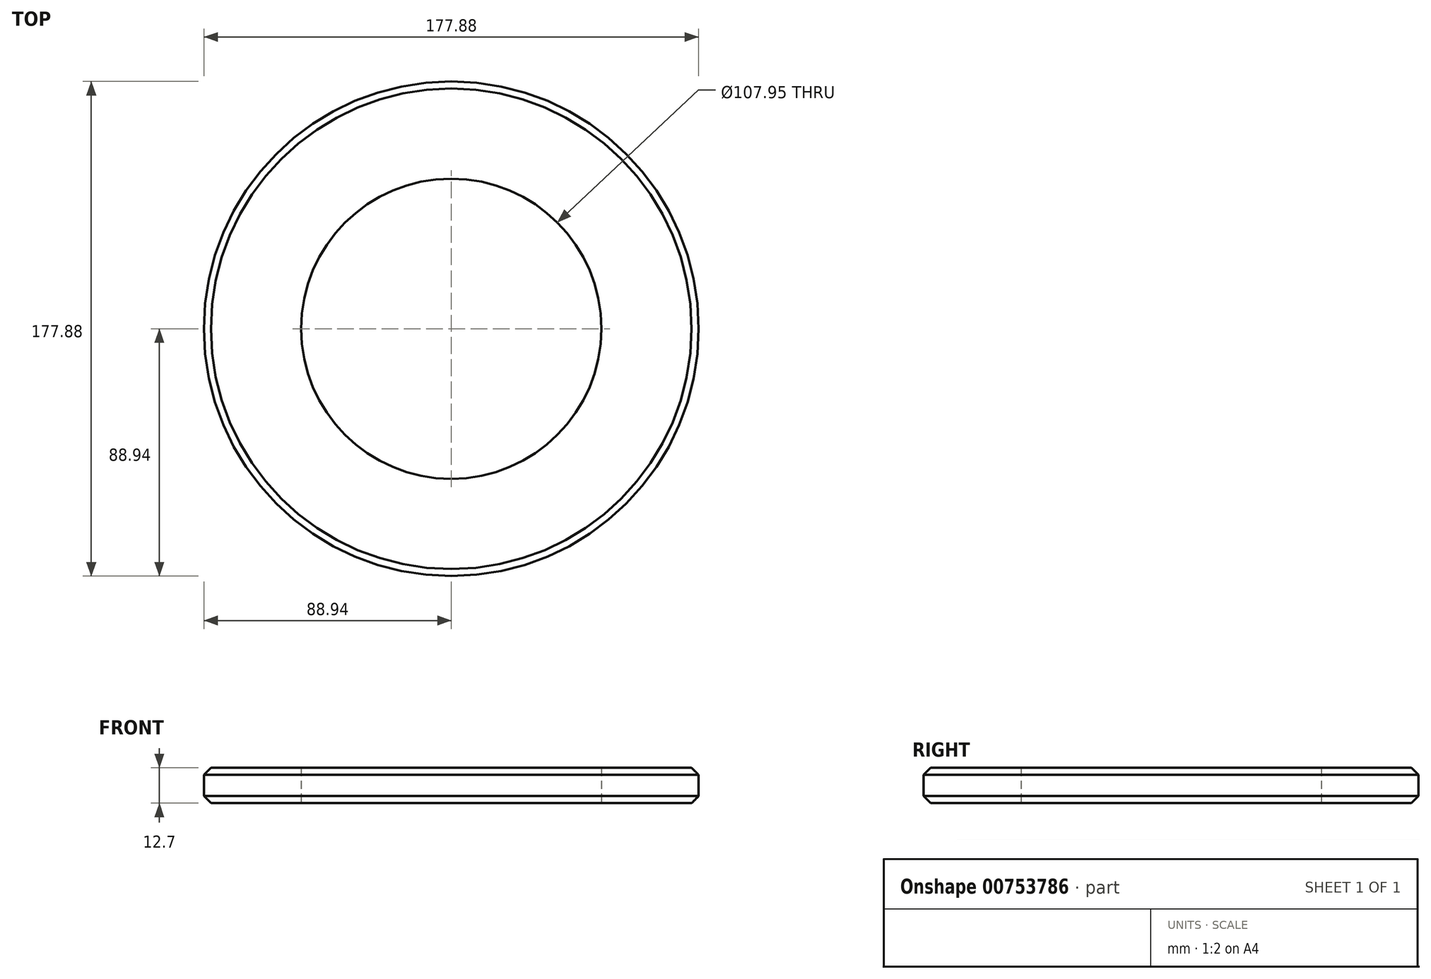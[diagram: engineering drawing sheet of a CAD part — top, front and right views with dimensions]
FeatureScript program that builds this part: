
annotation { "Feature Type Name" : "Feature", "Feature Type Description" : "" }
export const myFeature = defineFeature(function(context is Context, id is Id, definition is map)
    precondition{}
    {
        {
            var Q0;
            Q0=qCreatedBy(makeId("Top.planeOp"),FACE);
            var sketch = newSketch(context, id + "F0", { "sketchPlane" : qUnion([Q0])});
            skCircle(sketch, "E0", {"center": v(0, 0) * mm, "radius": 88.94 * mm});
            skSolve(sketch);
        }
        {
            var Q0;
            Q0 = qSketchRegion(id + "F0", true);
            extrude(context, id + "F1", {"entities" : qUnion([Q0]), "depth" : 12.7 * mm, "offsetDistance" : 25.4 * mm});
        }
        {
            var Q0;
            Q0=makeQuery(id+"F1.opExtrude","CAP_EDGE",EDGE,{"disambiguationData":[OSD([sQuery(id+"F0.wireOp",EDGE,"E0")])],"isStart":false});
            chamfer(context, id + "F2", {"entities" : qUnion([Q0]), "width" : 2.54 * mm, "tangentPropagation" : true});
        }
        {
            var Q0;
            Q0=makeQuery(id+"F1.opExtrude","CAP_EDGE",EDGE,{"disambiguationData":[OSD([sQuery(id+"F0.wireOp",EDGE,"E0")])],"isStart":true});
            chamfer(context, id + "F3", {"entities" : qUnion([Q0]), "width" : 2.54 * mm, "tangentPropagation" : true});
        }
        {
            var Q0;
            Q0=qCreatedBy(makeId("Top.planeOp"),FACE);
            var sketch = newSketch(context, id + "F4", { "sketchPlane" : qUnion([Q0])});
            skCircle(sketch, "E1", {"center": v(0, 0) * mm, "radius": 53.98 * mm});
            skSolve(sketch);
        }
        {
            var Q0;
            Q0 = qSketchRegion(id + "F4", true);
            extrude(context, id + "F5", {"entities" : qUnion([Q0]), "operationType" : NewBodyOperationType.REMOVE, "depth" : 50.8 * mm, "offsetDistance" : 25.4 * mm});
        }
    });
